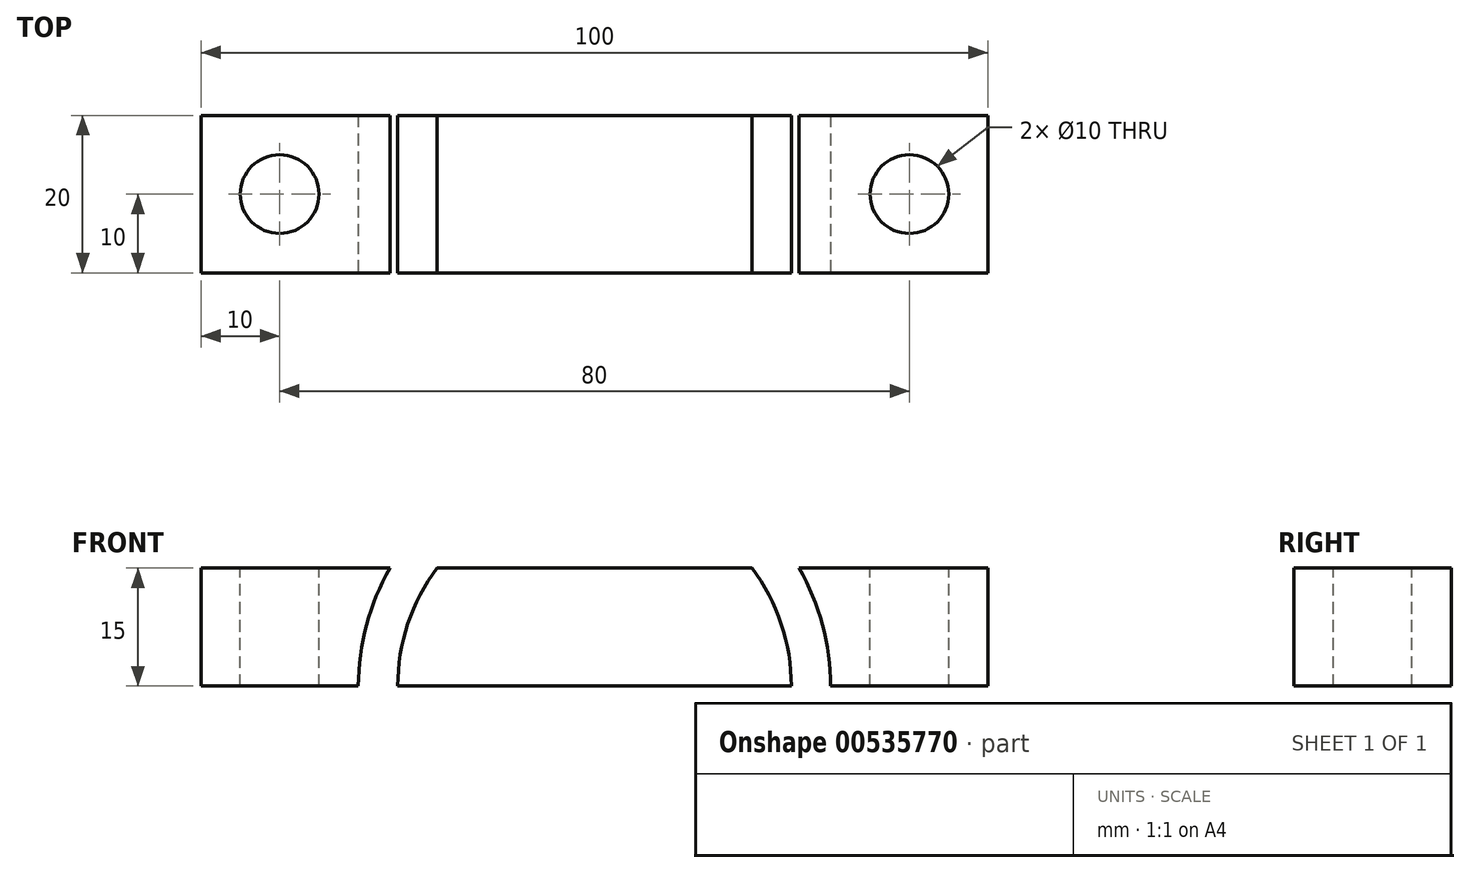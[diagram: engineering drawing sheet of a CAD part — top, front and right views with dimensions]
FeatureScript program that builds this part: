
annotation { "Feature Type Name" : "Feature", "Feature Type Description" : "" }
export const myFeature = defineFeature(function(context is Context, id is Id, definition is map)
    precondition{}
    {
        {
            var Q0;
            Q0=qCreatedBy(makeId("Front.planeOp"),FACE);
            var sketch = newSketch(context, id + "F0", { "sketchPlane" : qUnion([Q0])});
            skArc(sketch, "E0", {"start": v(-30, 0) * mm, "mid": v(-21.21, 21.21) * mm, "end": v(0, 30) * mm});
            skArc(sketch, "E1", {"start": v(-25, 0) * mm, "mid": v(-17.68, 17.68) * mm, "end": v(0, 25) * mm});
            skLineSegment(sketch, "E2", {"start": v(0, 30) * mm, "end": v(0, 0) * mm});
            skLineSegment(sketch, "E3", {"start": v(0, 0) * mm, "end": v(-30, 0) * mm});
            skSolve(sketch);
        }
        {
            var Q0;
            {var subQ0=sQuery(id+"F0.wireOp",EDGE,"E1");Q0=makeQuery(id+"F0.imprint","IMPRINT",FACE,{"disambiguationData":[TD([[makeQuery(id+"F0.imprint","IMPRINT",EDGE,{"derivedFrom":subQ0}),-1.0]])]});}
            var Q1;
            {var subQ0=sQuery(id+"F0.wireOp",EDGE,"E0");Q1=makeQuery(id+"F0.imprint","IMPRINT",FACE,{"disambiguationData":[TD([[makeQuery(id+"F0.imprint","IMPRINT",EDGE,{"derivedFrom":subQ0}),-1.0]])]});}
            extrude(context, id + "F1", {"entities" : qUnion([Q0, Q1]), "oppositeDirection" : true, "depth" : 60 * mm, "offsetDistance" : 25 * mm});
        }
        {
            var Q0;
            Q0=makeQuery(id+"F1.opExtrude","SWEPT_FACE",FACE,{"disambiguationData":[OSD([sQuery(id+"F0.wireOp",EDGE,"E2")])]});
            var sketch = newSketch(context, id + "F2", { "sketchPlane" : qUnion([Q0])});
            skLineSegment(sketch, "E4", {"start": v(60, 0) * mm, "end": v(40, 0) * mm});
            skLineSegment(sketch, "E5", {"start": v(40, 0) * mm, "end": v(40, 15) * mm});
            skLineSegment(sketch, "E6", {"start": v(40, 15) * mm, "end": v(60, 15) * mm});
            skLineSegment(sketch, "E7", {"start": v(60, 15) * mm, "end": v(60, 0) * mm});
            skSolve(sketch);
        }
        {
            var Q0;
            Q0=makeQuery(id+"F2.imprint","IMPRINT",FACE,{"disambiguationData":[TD([[makeQuery(id+"F2.imprint","IMPRINT",EDGE,{"derivedFrom":sQuery(id+"F2.wireOp",EDGE,"E4")}),-1.0]])]});
            extrude(context, id + "F3", {"entities" : qUnion([Q0]), "operationType" : NewBodyOperationType.ADD, "oppositeDirection" : true, "depth" : 50 * mm, "offsetDistance" : 25 * mm});
        }
        {
            var Q0;
            Q0=makeQuery(id+"F3.opExtrude","SWEPT_FACE",FACE,{"disambiguationData":[OSD([sQuery(id+"F2.wireOp",EDGE,"E6")])]});
            var sketch = newSketch(context, id + "F4", { "sketchPlane" : qUnion([Q0])});
            skLineSegment(sketch, "E8", {"start": v(-50, 60) * mm, "end": v(-50, 50) * mm});
            skLineSegment(sketch, "E9", {"start": v(-50, 50) * mm, "end": v(-40, 50) * mm});
            skLineSegment(sketch, "E10", {"start": v(-40, 50) * mm, "end": v(0, 50) * mm});
            skCircle(sketch, "E11", {"center": v(-40, 50) * mm, "radius": 5 * mm});
            skLineSegment(sketch, "E12", {"start": v(-40, 50) * mm, "end": v(-40, 40) * mm});
            skLineSegment(sketch, "E13", {"start": v(-40, 40) * mm, "end": v(-25.98, 40) * mm});
            skLineSegment(sketch, "E14", {"start": v(-40, 50) * mm, "end": v(-40, 60) * mm});
            skLineSegment(sketch, "E15", {"start": v(-40, 60) * mm, "end": v(-25.98, 60) * mm});
            skArc(sketch, "E16", {"start": v(-40, 40) * mm, "mid": v(-50, 50) * mm, "end": v(-40, 60) * mm});
            skSolve(sketch);
        }
        {
            var Q0;
            {var subQ0=sQuery(id+"F0.wireOp",EDGE,"E1");Q0=makeQuery(id+"F0.imprint","IMPRINT",FACE,{"disambiguationData":[TD([[makeQuery(id+"F0.imprint","IMPRINT",EDGE,{"derivedFrom":subQ0}),-1.0]])]});}
            extrude(context, id + "F5", {"entities" : qUnion([Q0]), "operationType" : NewBodyOperationType.REMOVE, "endBound" : BoundingType.THROUGH_ALL, "oppositeDirection" : true, "depth" : 25 * mm, "offsetDistance" : 25 * mm});
        }
        {
            var Q0;
            Q0=qCreatedBy(makeId("Top.planeOp"),FACE);
            var sketch = newSketch(context, id + "F6", { "sketchPlane" : qUnion([Q0])});
            skLineSegment(sketch, "E17", {"start": v(0, 0) * mm, "end": v(-10, 0) * mm});
            skLineSegment(sketch, "E18", {"start": v(-10, 0) * mm, "end": v(-10, 20) * mm});
            skLineSegment(sketch, "E19", {"start": v(0, 0) * mm, "end": v(0, 20) * mm});
            skLineSegment(sketch, "E20", {"start": v(0, 20) * mm, "end": v(-10, 20) * mm});
            skArc(sketch, "E21", {"start": v(-10, 20) * mm, "mid": v(-7.07, 27.07) * mm, "end": v(0, 30) * mm});
            skLineSegment(sketch, "E22", {"start": v(0, 30) * mm, "end": v(0, 20) * mm});
            skSolve(sketch);
        }
        {
            var Q0;
            Q0=qSketchRegion(id+"F6",true);
            extrude(context, id + "F7", {"entities" : qUnion([Q0]), "operationType" : NewBodyOperationType.REMOVE, "endBound" : BoundingType.THROUGH_ALL, "depth" : 25 * mm, "offsetDistance" : 25 * mm});
        }
        {
            var Q0;
            {var subQ1=sQuery(id+"F2.wireOp",EDGE,"E6");var subQ2=makeQuery(id+"F3.opExtrude","CAP_EDGE",EDGE,{"disambiguationData":[OSD([subQ1])],"isStart":false});var subQ4=makeQuery(id+"F3.opExtrude","SWEPT_EDGE",EDGE,{"disambiguationData":[OSD([sQuery(id+"F2.wireOp",EDGE,"E5"),subQ1])]});var subQ6=makeQuery(id+"F4.imprint","INTERSECT",VERTEX,{"derivedFrom":[subQ2,subQ4]});Q0=makeQuery(id+"F4.imprint","IMPRINT",FACE,{"disambiguationData":[TD([[makeQuery(id+"F4.imprint","IMPRINT",EDGE,{"disambiguationData":[TD([[subQ6,-1.0]])],"derivedFrom":subQ2}),-1.0]])]});}
            var Q1;
            {var subQ0=sQuery(id+"F4.wireOp",EDGE,"E8");Q1=makeQuery(id+"F4.imprint","IMPRINT",FACE,{"disambiguationData":[TD([[makeQuery(id+"F4.imprint","IMPRINT",EDGE,{"derivedFrom":subQ0}),-1.0]])]});}
            var Q2;
            {var subQ1=sQuery(id+"F4.wireOp",EDGE,"E9");var subQ3=sQuery(id+"F4.wireOp",EDGE,"E11");var subQ4=makeQuery(id+"F4.imprint","INTERSECT",VERTEX,{"derivedFrom":[subQ1,subQ3]});Q2=makeQuery(id+"F4.imprint","IMPRINT",FACE,{"disambiguationData":[TD([[makeQuery(id+"F4.imprint","IMPRINT",EDGE,{"disambiguationData":[TD([[subQ4,-1.0]])],"derivedFrom":subQ3}),1.0]])]});}
            var Q3;
            {var subQ1=sQuery(id+"F4.wireOp",EDGE,"E10");var subQ3=sQuery(id+"F4.wireOp",EDGE,"E11");var subQ4=makeQuery(id+"F4.imprint","INTERSECT",VERTEX,{"derivedFrom":[subQ1,subQ3]});Q3=makeQuery(id+"F4.imprint","IMPRINT",FACE,{"disambiguationData":[TD([[makeQuery(id+"F4.imprint","IMPRINT",EDGE,{"disambiguationData":[TD([[subQ4,1.0]])],"derivedFrom":subQ3}),1.0]])]});}
            var Q4;
            {var subQ1=sQuery(id+"F4.wireOp",EDGE,"E10");var subQ3=sQuery(id+"F4.wireOp",EDGE,"E11");var subQ4=makeQuery(id+"F4.imprint","INTERSECT",VERTEX,{"derivedFrom":[subQ1,subQ3]});Q4=makeQuery(id+"F4.imprint","IMPRINT",FACE,{"disambiguationData":[TD([[makeQuery(id+"F4.imprint","IMPRINT",EDGE,{"disambiguationData":[TD([[subQ4,-1.0]])],"derivedFrom":subQ3}),1.0]])]});}
            var Q5;
            {var subQ1=sQuery(id+"F4.wireOp",EDGE,"E9");var subQ3=sQuery(id+"F4.wireOp",EDGE,"E11");var subQ4=makeQuery(id+"F4.imprint","INTERSECT",VERTEX,{"derivedFrom":[subQ1,subQ3]});Q5=makeQuery(id+"F4.imprint","IMPRINT",FACE,{"disambiguationData":[TD([[makeQuery(id+"F4.imprint","IMPRINT",EDGE,{"disambiguationData":[TD([[subQ4,1.0]])],"derivedFrom":subQ3}),1.0]])]});}
            extrude(context, id + "F8", {"entities" : qUnion([Q0, Q1, Q2, Q3, Q4, Q5]), "operationType" : NewBodyOperationType.REMOVE, "endBound" : BoundingType.THROUGH_ALL, "oppositeDirection" : true, "depth" : 25 * mm, "offsetDistance" : 25 * mm});
        }
        {
            var Q0;
            Q0=makeQuery(id+"F1.opExtrude","SWEPT_BODY",BODY,{"disambiguationData":[OSD([sQuery(id+"F0.wireOp",EDGE,"E0"),sQuery(id+"F0.wireOp",EDGE,"E2"),sQuery(id+"F0.wireOp",EDGE,"E3")])]});
            var Q1;
            Q1=qCreatedBy(makeId("Right.planeOp"),FACE);
            mirror(context, id + "F9", {"operationType" : NewBodyOperationType.ADD, "entities" : qUnion([Q0]), "mirrorPlane" : qUnion([Q1])});
        }
    });
